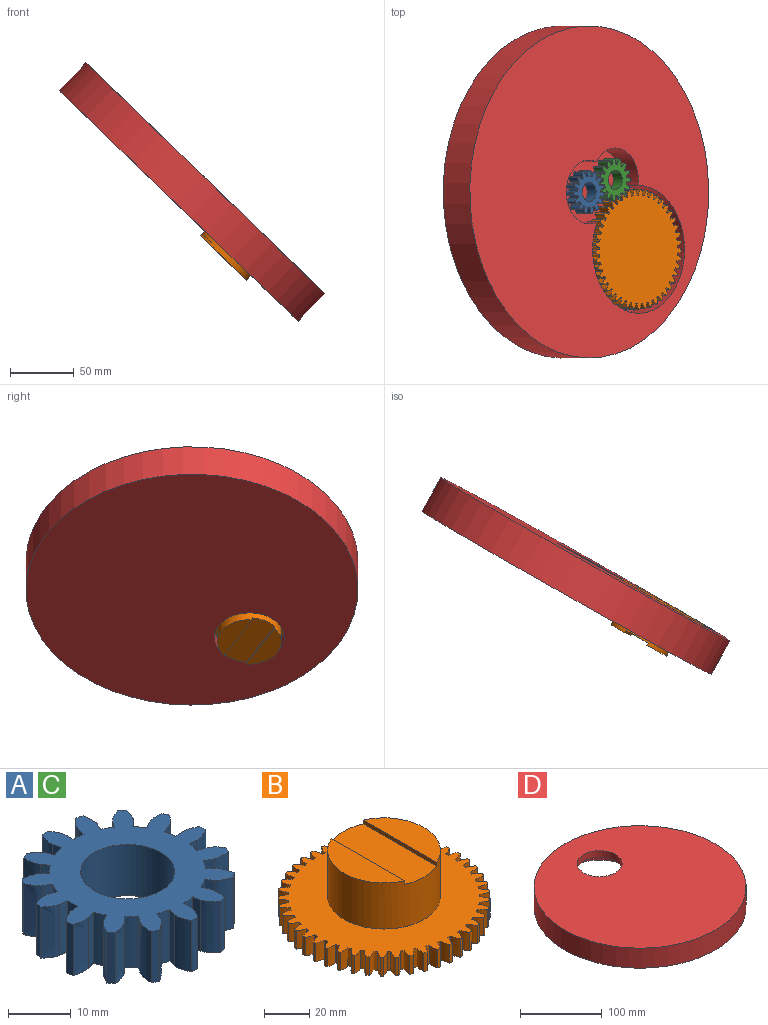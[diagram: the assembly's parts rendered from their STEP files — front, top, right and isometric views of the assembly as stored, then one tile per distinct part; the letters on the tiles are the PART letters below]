
ASSEMBLY  parts=4 mates=6
PART A: 93 faces, bbox 33.8x33.9x10 mm
  f0: cylinder r=7.5mm len=15mm, axis (0,0,1), area 471.2mm2, adj f91,f92
  f1: plane 10x1.52mm, normal (0.29,0.96,0), area 16mm2, adj f2,f90,f91,f92
  f2: extruded ~10x2.32mm, area 32mm2, adj f1,f3,f91,f92
  f3: cylinder r=17mm len=10mm, axis (0,0,1), area 13.1mm2, adj f2,f4,f91,f92
  f4: extruded ~10x3.15mm, area 32mm2, adj f3,f5,f91,f92
  f5: plane 10x1.37mm, normal (-0.51,-0.86,0), area 16mm2, adj f4,f6,f91,f92
  f6: cylinder r=12.5mm len=10mm, axis (0,0,1), area 22.5mm2, adj f5,f7,f91,f92
  f7: plane 10x1.2mm, normal (0.66,0.75,0), area 16mm2, adj f6,f8,f91,f92
  f8: extruded ~10x2.91mm, area 32mm2, adj f7,f9,f91,f92
  f9: cylinder r=17mm len=10mm, axis (0,0,1), area 13.1mm2, adj f8,f10,f91,f92
  f10: extruded ~10x2.77mm, area 32mm2, adj f9,f11,f91,f92
  f11: plane 10x1.3mm, normal (-0.82,-0.58,0), area 16mm2, adj f10,f12,f91,f92
  f12: cylinder r=12.5mm len=10mm, axis (0,0,1), area 22.5mm2, adj f11,f13,f91,f92
  f13: plane 10x1.45mm, normal (0.91,0.42,0), area 16mm2, adj f12,f14,f91,f92
  f14: extruded ~10x3.16mm, area 32mm2, adj f13,f15,f91,f92
  f15: cylinder r=17mm len=10mm, axis (0,0,1), area 13.1mm2, adj f14,f16,f91,f92
  f16: extruded ~10x2.53mm, area 32mm2, adj f15,f17,f91,f92
  f17: plane 10x1.57mm, normal (-0.98,-0.19,0), area 16mm2, adj f16,f18,f91,f92
  f18: cylinder r=12.5mm len=10mm, axis (0,0,1), area 22.5mm2, adj f17,f19,f91,f92
  f19: plane 10x1.6mm, normal (1,0.01,0), area 16mm2, adj f18,f20,f91,f92
  f20: extruded ~10x2.87mm, area 32mm2, adj f19,f21,f91,f92
  f21: cylinder r=17mm len=10mm, axis (0,0,1), area 13.1mm2, adj f20,f22,f91,f92
  f22: extruded ~10x3.08mm, area 32mm2, adj f21,f23,f91,f92
  f23: plane 10x1.56mm, normal (-0.97,0.22,0), area 16mm2, adj f22,f24,f91,f92
  f24: cylinder r=12.5mm len=10mm, axis (0,0,1), area 22.5mm2, adj f23,f25,f91,f92
  f25: plane 10x1.47mm, normal (0.92,-0.39,0), area 16mm2, adj f24,f26,f91,f92
  f26: extruded ~10x2.38mm, area 32mm2, adj f25,f27,f91,f92
  f27: cylinder r=17mm len=10mm, axis (0,0,1), area 13.1mm2, adj f26,f28,f91,f92
  f28: extruded ~10x3.1mm, area 32mm2, adj f27,f29,f91,f92
  f29: plane 10x1.28mm, normal (-0.8,0.6,0), area 16mm2, adj f28,f30,f91,f92
  f30: cylinder r=12.5mm len=10mm, axis (0,0,1), area 22.5mm2, adj f29,f31,f91,f92
  f31: plane 10x1.17mm, normal (0.68,-0.73,0), area 16mm2, adj f30,f32,f91,f92
  f32: extruded ~10x3.02mm, area 32mm2, adj f31,f33,f91,f92
  f33: cylinder r=17mm len=10mm, axis (0,0,1), area 13.1mm2, adj f32,f34,f91,f92
  f34: extruded ~10x2.59mm, area 32mm2, adj f33,f35,f91,f92
  f35: plane 10x1.39mm, normal (-0.49,0.87,0), area 16mm2, adj f34,f36,f91,f92
  f36: cylinder r=12.5mm len=10mm, axis (0,0,1), area 22.5mm2, adj f35,f37,f91,f92
  f37: plane 10x1.51mm, normal (0.32,-0.95,0), area 16mm2, adj f36,f38,f91,f92
  f38: extruded ~10x3.14mm, area 32mm2, adj f37,f39,f91,f92
  f39: cylinder r=17mm len=10mm, axis (0,0,1), area 13.1mm2, adj f38,f40,f91,f92
  f40: extruded ~10x2.71mm, area 32mm2, adj f39,f41,f91,f92
  f41: plane 10x1.59mm, normal (-0.09,1,0), area 16mm2, adj f40,f42,f91,f92
  f42: cylinder r=12.5mm len=10mm, axis (0,0,1), area 22.5mm2, adj f41,f43,f91,f92
  f43: plane 10x1.59mm, normal (-0.09,-1,0), area 16mm2, adj f42,f44,f91,f92
  f44: extruded ~10x2.71mm, area 32mm2, adj f43,f45,f91,f92
  f45: cylinder r=17mm len=10mm, axis (0,0,1), area 13.1mm2, adj f44,f46,f91,f92
  f46: extruded ~10x3.14mm, area 32mm2, adj f45,f47,f91,f92
  f47: plane 10x1.51mm, normal (0.32,0.95,0), area 16mm2, adj f46,f48,f91,f92
  f48: cylinder r=12.5mm len=10mm, axis (0,0,1), area 22.5mm2, adj f47,f49,f91,f92
  f49: plane 10x1.39mm, normal (-0.49,-0.87,0), area 16mm2, adj f48,f50,f91,f92
  f50: extruded ~10x2.59mm, area 32mm2, adj f49,f51,f91,f92
  f51: cylinder r=17mm len=10mm, axis (0,0,1), area 13.1mm2, adj f50,f52,f91,f92
  f52: extruded ~10x3.02mm, area 32mm2, adj f51,f53,f91,f92
  f53: plane 10x1.17mm, normal (0.68,0.73,0), area 16mm2, adj f52,f54,f91,f92
  f54: cylinder r=12.5mm len=10mm, axis (0,0,1), area 22.5mm2, adj f53,f55,f91,f92
  f55: plane 10x1.28mm, normal (-0.8,-0.6,0), area 16mm2, adj f54,f56,f91,f92
  f56: extruded ~10x3.1mm, area 32mm2, adj f55,f57,f91,f92
  f57: cylinder r=17mm len=10mm, axis (0,0,1), area 13.1mm2, adj f56,f58,f91,f92
  f58: extruded ~10x2.38mm, area 32mm2, adj f57,f59,f91,f92
  f59: plane 10x1.47mm, normal (0.92,0.39,0), area 16mm2, adj f58,f60,f91,f92
  f60: cylinder r=12.5mm len=10mm, axis (0,0,1), area 22.5mm2, adj f59,f61,f91,f92
  f61: plane 10x1.56mm, normal (-0.97,-0.22,0), area 16mm2, adj f60,f62,f91,f92
  f62: extruded ~10x3.08mm, area 32mm2, adj f61,f63,f91,f92
  f63: cylinder r=17mm len=10mm, axis (0,0,1), area 13.1mm2, adj f62,f64,f91,f92
  f64: extruded ~10x2.87mm, area 32mm2, adj f63,f65,f91,f92
  f65: plane 10x1.6mm, normal (1,-0.01,0), area 16mm2, adj f64,f66,f91,f92
  f66: cylinder r=12.5mm len=10mm, axis (0,0,1), area 22.5mm2, adj f65,f67,f91,f92
  f67: plane 10x1.57mm, normal (-0.98,0.19,0), area 16mm2, adj f66,f68,f91,f92
  f68: extruded ~10x2.53mm, area 32mm2, adj f67,f69,f91,f92
  f69: cylinder r=17mm len=10mm, axis (0,0,1), area 13.1mm2, adj f68,f70,f91,f92
  f70: extruded ~10x3.16mm, area 32mm2, adj f69,f71,f91,f92
  f71: plane 10x1.45mm, normal (0.91,-0.42,0), area 16mm2, adj f70,f72,f91,f92
  f72: cylinder r=12.5mm len=10mm, axis (0,0,1), area 22.5mm2, adj f71,f73,f91,f92
  f73: plane 10x1.3mm, normal (-0.82,0.58,0), area 16mm2, adj f72,f74,f91,f92
  f74: extruded ~10x2.77mm, area 32mm2, adj f73,f75,f91,f92
  f75: cylinder r=17mm len=10mm, axis (0,0,1), area 13.1mm2, adj f74,f76,f91,f92
  f76: extruded ~10x2.91mm, area 32mm2, adj f75,f77,f91,f92
  f77: plane 10x1.2mm, normal (0.66,-0.75,0), area 16mm2, adj f76,f78,f91,f92
  f78: cylinder r=12.5mm len=10mm, axis (0,0,1), area 22.5mm2, adj f77,f79,f91,f92
  f79: plane 10x1.37mm, normal (-0.51,0.86,0), area 16mm2, adj f78,f80,f91,f92
  f80: extruded ~10x3.15mm, area 32mm2, adj f79,f81,f91,f92
  f81: cylinder r=17mm len=10mm, axis (0,0,1), area 13.1mm2, adj f80,f82,f91,f92
  f82: extruded ~10x2.32mm, area 32mm2, adj f81,f83,f91,f92
  f83: plane 10x1.52mm, normal (0.29,-0.96,0), area 16mm2, adj f82,f84,f91,f92
  f84: cylinder r=12.5mm len=10mm, axis (0,0,1), area 22.5mm2, adj f83,f85,f91,f92
  f85: plane 10x1.58mm, normal (-0.12,0.99,0), area 16mm2, adj f84,f86,f91,f92
  f86: extruded ~10x2.99mm, area 32mm2, adj f85,f87,f91,f92
  f87: cylinder r=17mm len=10mm, axis (0,0,1), area 13.1mm2, adj f86,f88,f91,f92
  f88: extruded ~10x2.99mm, area 32mm2, adj f87,f89,f91,f92
  f89: plane 10x1.58mm, normal (-0.12,-0.99,0), area 16mm2, adj f88,f90,f91,f92
  f90: cylinder r=12.5mm len=10mm, axis (0,0,1), area 22.5mm2, adj f1,f89,f91,f92
  f91: plane 33.93x33.75mm, normal (0,0,1), area 505.5mm2, adj f0,f1,f2,f3,f4,f5,f6,f7
  f92: plane 33.93x33.75mm, normal (0,0,-1), area 505.5mm2, adj f0,f1,f2,f3,f4,f5,f6,f7
PART B: 188 faces, bbox 93.9x94x35 mm
  f0: plane 45.83x2mm, normal (-1,0,0), area 91.7mm2, adj f2,f4,f5
  f1: plane 45.83x2mm, normal (1,0,0), area 91.7mm2, adj f2,f3,f5
  f2: plane 50x20mm, normal (0,0,1), area 972.7mm2, adj f0,f1,f5
  f3: plane 45.83x15mm, normal (0,0,1), area 495.4mm2, adj f1,f5
  f4: plane 45.83x15mm, normal (0,0,1), area 495.4mm2, adj f0,f5
  f5: cylinder r=25mm len=50mm, axis (0,0,1), area 3844.7mm2, adj f0,f1,f2,f3,f4,f186
  f6: extruded ~10x4.32mm, area 47.6mm2, adj f7,f185,f186,f187
  f7: cylinder r=47mm len=10mm, axis (0,0,1), area 15.4mm2, adj f6,f8,f186,f187
  f8: extruded ~10x4.69mm, area 47.6mm2, adj f7,f9,f186,f187
  f9: cylinder r=42.5mm len=10mm, axis (0,0,1), area 17.3mm2, adj f8,f10,f186,f187
  f10: extruded ~10x4mm, area 47.6mm2, adj f9,f11,f186,f187
  f11: cylinder r=47mm len=10mm, axis (0,0,1), area 15.4mm2, adj f10,f12,f186,f187
  f12: extruded ~10x4.74mm, area 47.6mm2, adj f11,f13,f186,f187
  f13: cylinder r=42.5mm len=10mm, axis (0,0,1), area 17.3mm2, adj f12,f14,f186,f187
  f14: extruded ~10x3.61mm, area 47.6mm2, adj f13,f15,f186,f187
  f15: cylinder r=47mm len=10mm, axis (0,0,1), area 15.4mm2, adj f14,f16,f186,f187
  f16: extruded ~10x4.7mm, area 47.6mm2, adj f15,f17,f186,f187
  f17: cylinder r=42.5mm len=10mm, axis (0,0,1), area 17.3mm2, adj f16,f18,f186,f187
  f18: extruded ~10x3.54mm, area 47.6mm2, adj f17,f19,f186,f187
  f19: cylinder r=47mm len=10mm, axis (0,0,1), area 15.4mm2, adj f18,f20,f186,f187
  f20: extruded ~10x4.56mm, area 47.6mm2, adj f19,f21,f186,f187
  f21: cylinder r=42.5mm len=10mm, axis (0,0,1), area 17.3mm2, adj f20,f22,f186,f187
  f22: extruded ~10x3.94mm, area 47.6mm2, adj f21,f23,f186,f187
  f23: cylinder r=47mm len=10mm, axis (0,0,1), area 15.4mm2, adj f22,f24,f186,f187
  f24: extruded ~10x4.34mm, area 47.6mm2, adj f23,f25,f186,f187
  f25: cylinder r=42.5mm len=10mm, axis (0,0,1), area 17.3mm2, adj f24,f26,f186,f187
  f26: extruded ~10x4.27mm, area 47.6mm2, adj f25,f27,f186,f187
  f27: cylinder r=47mm len=10mm, axis (0,0,1), area 15.4mm2, adj f26,f28,f186,f187
  f28: extruded ~10x4.03mm, area 47.6mm2, adj f27,f29,f186,f187
  f29: cylinder r=42.5mm len=10mm, axis (0,0,1), area 17.3mm2, adj f28,f30,f186,f187
  f30: extruded ~10x4.51mm, area 47.6mm2, adj f29,f31,f186,f187
  f31: cylinder r=47mm len=10mm, axis (0,0,1), area 15.4mm2, adj f30,f32,f186,f187
  f32: extruded ~10x3.65mm, area 47.6mm2, adj f31,f33,f186,f187
  f33: cylinder r=42.5mm len=10mm, axis (0,0,1), area 17.3mm2, adj f32,f34,f186,f187
  f34: extruded ~10x4.67mm, area 47.6mm2, adj f33,f35,f186,f187
  f35: cylinder r=47mm len=10mm, axis (0,0,1), area 15.4mm2, adj f34,f36,f186,f187
  f36: extruded ~10x3.5mm, area 47.6mm2, adj f35,f37,f186,f187
  f37: cylinder r=42.5mm len=10mm, axis (0,0,1), area 17.3mm2, adj f36,f38,f186,f187
  f38: extruded ~10x4.74mm, area 47.6mm2, adj f37,f39,f186,f187
  f39: cylinder r=47mm len=10mm, axis (0,0,1), area 15.4mm2, adj f38,f40,f186,f187
  f40: extruded ~10x3.91mm, area 47.6mm2, adj f39,f41,f186,f187
  f41: cylinder r=42.5mm len=10mm, axis (0,0,1), area 17.3mm2, adj f40,f42,f186,f187
  f42: extruded ~10x4.71mm, area 47.6mm2, adj f41,f43,f186,f187
  f43: cylinder r=47mm len=10mm, axis (0,0,1), area 15.4mm2, adj f42,f44,f186,f187
  f44: extruded ~10x4.25mm, area 47.6mm2, adj f43,f45,f186,f187
  f45: cylinder r=42.5mm len=10mm, axis (0,0,1), area 17.3mm2, adj f44,f46,f186,f187
  f46: extruded ~10x4.59mm, area 47.6mm2, adj f45,f47,f186,f187
  f47: cylinder r=47mm len=10mm, axis (0,0,1), area 15.4mm2, adj f46,f48,f186,f187
  f48: extruded ~10x4.5mm, area 47.6mm2, adj f47,f49,f186,f187
  f49: cylinder r=42.5mm len=10mm, axis (0,0,1), area 17.3mm2, adj f48,f50,f186,f187
  f50: extruded ~10x4.38mm, area 47.6mm2, adj f49,f51,f186,f187
  f51: cylinder r=47mm len=10mm, axis (0,0,1), area 15.4mm2, adj f50,f52,f186,f187
  f52: extruded ~10x4.66mm, area 47.6mm2, adj f51,f53,f186,f187
  f53: cylinder r=42.5mm len=10mm, axis (0,0,1), area 17.3mm2, adj f52,f54,f186,f187
  f54: extruded ~10x4.09mm, area 47.6mm2, adj f53,f55,f186,f187
  f55: cylinder r=47mm len=10mm, axis (0,0,1), area 15.4mm2, adj f54,f56,f186,f187
  f56: extruded ~10x4.73mm, area 47.6mm2, adj f55,f57,f186,f187
  f57: cylinder r=42.5mm len=10mm, axis (0,0,1), area 17.3mm2, adj f56,f58,f186,f187
  f58: extruded ~10x3.72mm, area 47.6mm2, adj f57,f59,f186,f187
  f59: cylinder r=47mm len=10mm, axis (0,0,1), area 15.4mm2, adj f58,f60,f186,f187
  f60: extruded ~10x4.71mm, area 47.6mm2, adj f59,f61,f186,f187
  f61: cylinder r=42.5mm len=10mm, axis (0,0,1), area 17.3mm2, adj f60,f62,f186,f187
  f62: extruded ~10x3.43mm, area 47.6mm2, adj f61,f63,f186,f187
  f63: cylinder r=47mm len=10mm, axis (0,0,1), area 15.4mm2, adj f62,f64,f186,f187
  f64: extruded ~10x4.6mm, area 47.6mm2, adj f63,f65,f186,f187
  f65: cylinder r=42.5mm len=10mm, axis (0,0,1), area 17.3mm2, adj f64,f66,f186,f187
  f66: extruded ~10x3.85mm, area 47.6mm2, adj f65,f67,f186,f187
  f67: cylinder r=47mm len=10mm, axis (0,0,1), area 15.4mm2, adj f66,f68,f186,f187
  f68: extruded ~10x4.4mm, area 47.6mm2, adj f67,f69,f186,f187
  f69: cylinder r=42.5mm len=10mm, axis (0,0,1), area 17.3mm2, adj f68,f70,f186,f187
  f70: extruded ~10x4.2mm, area 47.6mm2, adj f69,f71,f186,f187
  f71: cylinder r=47mm len=10mm, axis (0,0,1), area 15.4mm2, adj f70,f72,f186,f187
  f72: extruded ~10x4.12mm, area 47.6mm2, adj f71,f73,f186,f187
  f73: cylinder r=42.5mm len=10mm, axis (0,0,1), area 17.3mm2, adj f72,f74,f186,f187
  f74: extruded ~10x4.46mm, area 47.6mm2, adj f73,f75,f186,f187
  f75: cylinder r=47mm len=10mm, axis (0,0,1), area 15.4mm2, adj f74,f76,f186,f187
  f76: extruded ~10x3.75mm, area 47.6mm2, adj f75,f77,f186,f187
  f77: cylinder r=42.5mm len=10mm, axis (0,0,1), area 17.3mm2, adj f76,f78,f186,f187
  f78: extruded ~10x4.64mm, area 47.6mm2, adj f77,f79,f186,f187
  f79: cylinder r=47mm len=10mm, axis (0,0,1), area 15.4mm2, adj f78,f80,f186,f187
  f80: extruded ~10x3.39mm, area 47.6mm2, adj f79,f81,f186,f187
  f81: cylinder r=42.5mm len=10mm, axis (0,0,1), area 17.3mm2, adj f80,f82,f186,f187
  f82: extruded ~10x4.73mm, area 47.6mm2, adj f81,f83,f186,f187
  f83: cylinder r=47mm len=10mm, axis (0,0,1), area 15.4mm2, adj f82,f84,f186,f187
  f84: extruded ~10x3.82mm, area 47.6mm2, adj f83,f85,f186,f187
  f85: cylinder r=42.5mm len=10mm, axis (0,0,1), area 17.3mm2, adj f84,f86,f186,f187
  f86: extruded ~10x4.72mm, area 47.6mm2, adj f85,f87,f186,f187
  f87: cylinder r=47mm len=10mm, axis (0,0,1), area 15.4mm2, adj f86,f88,f186,f187
  f88: extruded ~10x4.17mm, area 47.6mm2, adj f87,f89,f186,f187
  f89: cylinder r=42.5mm len=10mm, axis (0,0,1), area 17.3mm2, adj f88,f90,f186,f187
  f90: extruded ~10x4.63mm, area 47.6mm2, adj f89,f91,f186,f187
  f91: cylinder r=47mm len=10mm, axis (0,0,1), area 15.4mm2, adj f90,f92,f186,f187
  f92: extruded ~10x4.44mm, area 47.6mm2, adj f91,f93,f186,f187
  f93: cylinder r=42.5mm len=10mm, axis (0,0,1), area 17.3mm2, adj f92,f94,f186,f187
  f94: extruded ~10x4.44mm, area 47.6mm2, adj f93,f95,f186,f187
  f95: cylinder r=47mm len=10mm, axis (0,0,1), area 15.4mm2, adj f94,f96,f186,f187
  f96: extruded ~10x4.63mm, area 47.6mm2, adj f95,f97,f186,f187
  f97: cylinder r=42.5mm len=10mm, axis (0,0,1), area 17.3mm2, adj f96,f98,f186,f187
  f98: extruded ~10x4.17mm, area 47.6mm2, adj f97,f99,f186,f187
  f99: cylinder r=47mm len=10mm, axis (0,0,1), area 15.4mm2, adj f98,f100,f186,f187
  f100: extruded ~10x4.72mm, area 47.6mm2, adj f99,f101,f186,f187
  f101: cylinder r=42.5mm len=10mm, axis (0,0,1), area 17.3mm2, adj f100,f102,f186,f187
  f102: extruded ~10x3.82mm, area 47.6mm2, adj f101,f103,f186,f187
  f103: cylinder r=47mm len=10mm, axis (0,0,1), area 15.4mm2, adj f102,f104,f186,f187
  f104: extruded ~10x4.73mm, area 47.6mm2, adj f103,f105,f186,f187
  f105: cylinder r=42.5mm len=10mm, axis (0,0,1), area 17.3mm2, adj f104,f106,f186,f187
  f106: extruded ~10x3.39mm, area 47.6mm2, adj f105,f107,f186,f187
  f107: cylinder r=47mm len=10mm, axis (0,0,1), area 15.4mm2, adj f106,f108,f186,f187
  f108: extruded ~10x4.64mm, area 47.6mm2, adj f107,f109,f186,f187
  f109: cylinder r=42.5mm len=10mm, axis (0,0,1), area 17.3mm2, adj f108,f110,f186,f187
  f110: extruded ~10x3.75mm, area 47.6mm2, adj f109,f111,f186,f187
  f111: cylinder r=47mm len=10mm, axis (0,0,1), area 15.4mm2, adj f110,f112,f186,f187
  f112: extruded ~10x4.46mm, area 47.6mm2, adj f111,f113,f186,f187
  f113: cylinder r=42.5mm len=10mm, axis (0,0,1), area 17.3mm2, adj f112,f114,f186,f187
  f114: extruded ~10x4.12mm, area 47.6mm2, adj f113,f115,f186,f187
  f115: cylinder r=47mm len=10mm, axis (0,0,1), area 15.4mm2, adj f114,f116,f186,f187
  f116: extruded ~10x4.2mm, area 47.6mm2, adj f115,f117,f186,f187
  f117: cylinder r=42.5mm len=10mm, axis (0,0,1), area 17.3mm2, adj f116,f118,f186,f187
  f118: extruded ~10x4.4mm, area 47.6mm2, adj f117,f119,f186,f187
  f119: cylinder r=47mm len=10mm, axis (0,0,1), area 15.4mm2, adj f118,f120,f186,f187
  f120: extruded ~10x3.85mm, area 47.6mm2, adj f119,f121,f186,f187
  f121: cylinder r=42.5mm len=10mm, axis (0,0,1), area 17.3mm2, adj f120,f122,f186,f187
  f122: extruded ~10x4.6mm, area 47.6mm2, adj f121,f123,f186,f187
  f123: cylinder r=47mm len=10mm, axis (0,0,1), area 15.4mm2, adj f122,f124,f186,f187
  f124: extruded ~10x3.43mm, area 47.6mm2, adj f123,f125,f186,f187
  f125: cylinder r=42.5mm len=10mm, axis (0,0,1), area 17.3mm2, adj f124,f126,f186,f187
  f126: extruded ~10x4.71mm, area 47.6mm2, adj f125,f127,f186,f187
  f127: cylinder r=47mm len=10mm, axis (0,0,1), area 15.4mm2, adj f126,f128,f186,f187
  f128: extruded ~10x3.72mm, area 47.6mm2, adj f127,f129,f186,f187
  f129: cylinder r=42.5mm len=10mm, axis (0,0,1), area 17.3mm2, adj f128,f130,f186,f187
  f130: extruded ~10x4.73mm, area 47.6mm2, adj f129,f131,f186,f187
  f131: cylinder r=47mm len=10mm, axis (0,0,1), area 15.4mm2, adj f130,f132,f186,f187
  f132: extruded ~10x4.09mm, area 47.6mm2, adj f131,f133,f186,f187
  f133: cylinder r=42.5mm len=10mm, axis (0,0,1), area 17.3mm2, adj f132,f134,f186,f187
  f134: extruded ~10x4.66mm, area 47.6mm2, adj f133,f135,f186,f187
  f135: cylinder r=47mm len=10mm, axis (0,0,1), area 15.4mm2, adj f134,f136,f186,f187
  f136: extruded ~10x4.38mm, area 47.6mm2, adj f135,f137,f186,f187
  f137: cylinder r=42.5mm len=10mm, axis (0,0,1), area 17.3mm2, adj f136,f138,f186,f187
  f138: extruded ~10x4.5mm, area 47.6mm2, adj f137,f139,f186,f187
  f139: cylinder r=47mm len=10mm, axis (0,0,1), area 15.4mm2, adj f138,f140,f186,f187
  f140: extruded ~10x4.59mm, area 47.6mm2, adj f139,f141,f186,f187
  f141: cylinder r=42.5mm len=10mm, axis (0,0,1), area 17.3mm2, adj f140,f142,f186,f187
  f142: extruded ~10x4.25mm, area 47.6mm2, adj f141,f143,f186,f187
  f143: cylinder r=47mm len=10mm, axis (0,0,1), area 15.4mm2, adj f142,f144,f186,f187
  f144: extruded ~10x4.71mm, area 47.6mm2, adj f143,f145,f186,f187
  f145: cylinder r=42.5mm len=10mm, axis (0,0,1), area 17.3mm2, adj f144,f146,f186,f187
  f146: extruded ~10x3.91mm, area 47.6mm2, adj f145,f147,f186,f187
  f147: cylinder r=47mm len=10mm, axis (0,0,1), area 15.4mm2, adj f146,f148,f186,f187
  f148: extruded ~10x4.74mm, area 47.6mm2, adj f147,f149,f186,f187
  f149: cylinder r=42.5mm len=10mm, axis (0,0,1), area 17.3mm2, adj f148,f150,f186,f187
  f150: extruded ~10x3.5mm, area 47.6mm2, adj f149,f151,f186,f187
  f151: cylinder r=47mm len=10mm, axis (0,0,1), area 15.4mm2, adj f150,f152,f186,f187
  f152: extruded ~10x4.67mm, area 47.6mm2, adj f151,f153,f186,f187
  f153: cylinder r=42.5mm len=10mm, axis (0,0,1), area 17.3mm2, adj f152,f154,f186,f187
  f154: extruded ~10x3.65mm, area 47.6mm2, adj f153,f155,f186,f187
  f155: cylinder r=47mm len=10mm, axis (0,0,1), area 15.4mm2, adj f154,f156,f186,f187
  f156: extruded ~10x4.51mm, area 47.6mm2, adj f155,f157,f186,f187
  f157: cylinder r=42.5mm len=10mm, axis (0,0,1), area 17.3mm2, adj f156,f158,f186,f187
  f158: extruded ~10x4.03mm, area 47.6mm2, adj f157,f159,f186,f187
  f159: cylinder r=47mm len=10mm, axis (0,0,1), area 15.4mm2, adj f158,f160,f186,f187
  f160: extruded ~10x4.27mm, area 47.6mm2, adj f159,f161,f186,f187
  f161: cylinder r=42.5mm len=10mm, axis (0,0,1), area 17.3mm2, adj f160,f162,f186,f187
  f162: extruded ~10x4.34mm, area 47.6mm2, adj f161,f163,f186,f187
  f163: cylinder r=47mm len=10mm, axis (0,0,1), area 15.4mm2, adj f162,f164,f186,f187
  f164: extruded ~10x3.94mm, area 47.6mm2, adj f163,f165,f186,f187
  f165: cylinder r=42.5mm len=10mm, axis (0,0,1), area 17.3mm2, adj f164,f166,f186,f187
  f166: extruded ~10x4.56mm, area 47.6mm2, adj f165,f167,f186,f187
  f167: cylinder r=47mm len=10mm, axis (0,0,1), area 15.4mm2, adj f166,f168,f186,f187
  f168: extruded ~10x3.54mm, area 47.6mm2, adj f167,f169,f186,f187
  f169: cylinder r=42.5mm len=10mm, axis (0,0,1), area 17.3mm2, adj f168,f170,f186,f187
  f170: extruded ~10x4.7mm, area 47.6mm2, adj f169,f171,f186,f187
  f171: cylinder r=47mm len=10mm, axis (0,0,1), area 15.4mm2, adj f170,f172,f186,f187
  f172: extruded ~10x3.61mm, area 47.6mm2, adj f171,f173,f186,f187
  f173: cylinder r=42.5mm len=10mm, axis (0,0,1), area 17.3mm2, adj f172,f174,f186,f187
  f174: extruded ~10x4.74mm, area 47.6mm2, adj f173,f175,f186,f187
  f175: cylinder r=47mm len=10mm, axis (0,0,1), area 15.4mm2, adj f174,f176,f186,f187
  f176: extruded ~10x4mm, area 47.6mm2, adj f175,f177,f186,f187
  f177: cylinder r=42.5mm len=10mm, axis (0,0,1), area 17.3mm2, adj f176,f178,f186,f187
  f178: extruded ~10x4.69mm, area 47.6mm2, adj f177,f179,f186,f187
  f179: cylinder r=47mm len=10mm, axis (0,0,1), area 15.4mm2, adj f178,f180,f186,f187
  f180: extruded ~10x4.32mm, area 47.6mm2, adj f179,f181,f186,f187
  f181: cylinder r=42.5mm len=10mm, axis (0,0,1), area 17.3mm2, adj f180,f182,f186,f187
  f182: extruded ~10x4.55mm, area 47.6mm2, adj f181,f183,f186,f187
  f183: cylinder r=47mm len=10mm, axis (0,0,1), area 15.4mm2, adj f182,f184,f186,f187
  f184: extruded ~10x4.55mm, area 47.6mm2, adj f183,f185,f186,f187
  f185: cylinder r=42.5mm len=10mm, axis (0,0,1), area 17.3mm2, adj f6,f184,f186,f187
  f186: plane 93.98x93.93mm, normal (0,0,1), area 4350.4mm2, adj f5,f6,f7,f8,f9,f10,f11,f12
  f187: plane 93.98x93.93mm, normal (0,0,-1), area 6313.9mm2, adj f6,f7,f8,f9,f10,f11,f12,f13
PART C: same geometry as A
PART D: 8 faces, bbox 260x260x30 mm
  f0: cylinder r=27.5mm len=55mm, axis (0,0,-1), area 1727.9mm2, adj f2,f4
  f1: plane 260x260mm, normal (0,0,-1), area 42346.3mm2, adj f3,f5,f6,f7
  f2: plane 260x260mm, normal (0,0,1), area 50717.1mm2, adj f0,f3
  f3: cylinder r=130mm len=260mm, axis (0,0,1), area 24504.4mm2, adj f1,f2
  f4: plane 145x100.56mm, normal (0,0,-1), area 8370.8mm2, adj f0,f5,f6,f7
  f5: cylinder r=25mm len=46.72mm, axis (0,0,1), area 1357.8mm2, adj f1,f4,f6,f7
  f6: cylinder r=25mm len=48.25mm, axis (0,0,1), area 1904.7mm2, adj f1,f4,f5,f7
  f7: cylinder r=50mm len=100mm, axis (0,0,1), area 5167.5mm2, adj f1,f4,f5,f6
PLACE A rot(axis=(-0.36,0.29,-0.89),109.6deg) t=(206.06,518.96,-172.01)mm
PLACE B rot(axis=(-0.5,-0.84,0.2),142.3deg) t=(251.6,473.99,-202.08)mm
PLACE C rot(axis=(-0.93,0,0.37),180deg) t=(233.48,528.45,-184.59)mm
PLACE D rot(axis=(-0.85,-0.4,0.34),161.8deg) t=(231.4,522.06,-196.48)mm
MATE cylindrical A.f0 <-> D.f3  axis (0.69,0,0.72) through (213.01,518.96,-164.82)mm
MATE cylindrical C.f0 <-> D.f5  axis (-0.69,0,-0.72) through (233.48,528.45,-184.59)mm
MATE planar A.f91 <-> B.f5  axis (0.69,0,0.72) through (221.21,513.83,-172.74)mm
MATE cylindrical D.f0 <-> B.f5  axis (-0.69,0,-0.72) through (230.76,473.99,-223.66)mm
MATE planar B.f187 <-> C.f92  axis (0.69,0,0.72) through (280.35,459.56,-229.85)mm
MATE planar D.f1 <-> B.f187  axis (0.69,0,0.72) through (205.31,526.84,-157.38)mm
